# Revit family: CB32
name_source: partatom
category: Lighting Fixtures
units: mm (PartAtom-declared; Revit-internal decimal feet)

## family parameters
Always vertical = Yes
Cut with Voids When Loaded = No
Light Source = Yes
OmniClass Number = 23.80.70.14
OmniClass Title = Luminaries for External Lighting
Part Type = Normal
Room Calculation Point = No
Round Connector Dimension = Use Diameter
Shared = No
Work Plane-Based = No

## types (1)
- CB
    Apparent Load = 0 VA
    Assembly Code = D5020200
    Color Filter = 16777215
    Default Elevation = 0 "
    Description = Compact Bollards feature full overlapping louvers which provides total source cutoff above horizontal. A soft glow from the louvers provides sufficient vertical illumination for gardens, pathways and of course, pedestrians.

Gasketed prismatic glass globe optimizes light output
Full cutoff above horizontal
Battery back-up, emergency battery pack and houseside shield options
    Diameter = 5 "
    Dimming Lamp Color Temperature Shift = <None>
    Finish = Powder Coat-White
    Glass = Glass-Temper Molded
    Height = 32 "
    Lamp = LED
    Load Classification = Lighting
    Manufacturer = Kim Lighting
    MasterFormat Title = Landscape Lighting, Site Lighting, Walkway Lighting
    Model = Compact Bollards
    Number of Poles = 1
    Photometric Notes = More IES files download on Photometric Web Link
    Photometric Web File = cb-20l4k.ies
    Power Factor = 1
    Radius = 2.5 "
    Series = Traditional Bollards
    Tilt Angle = 90.00°
    Type Comments = Lighted Bollard
    URL = https://www.currentlighting.com
    Voltage = 120 V
    Wattage Comments = default

## geometry (parser evidence)
native form markers: Sweep x2
no freeform markers — native parametric forms only
